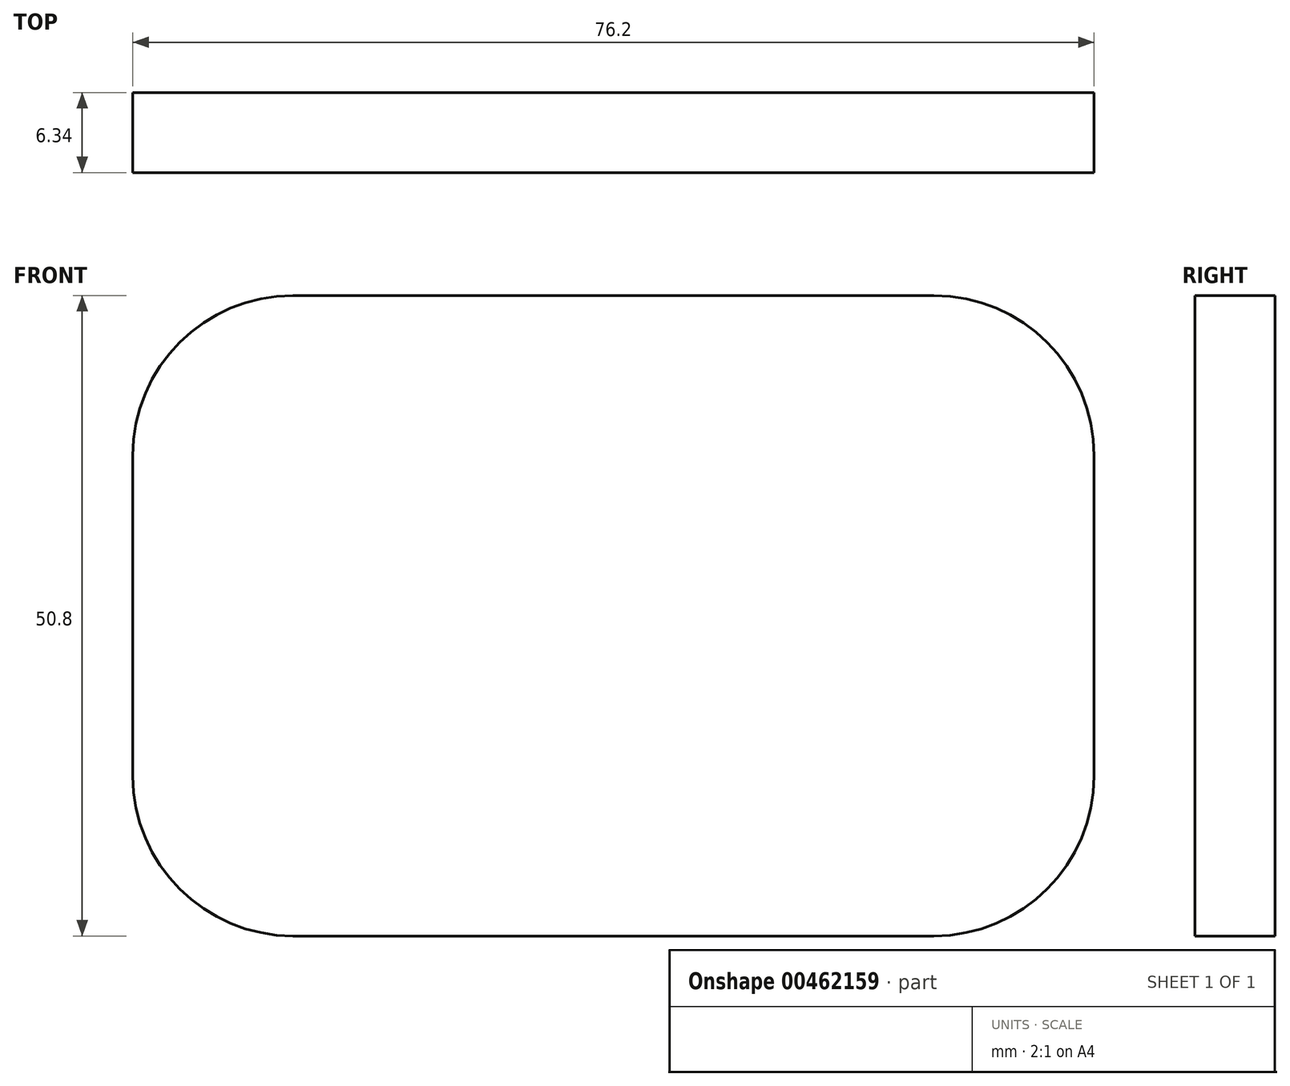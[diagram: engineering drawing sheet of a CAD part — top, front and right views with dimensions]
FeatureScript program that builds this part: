
annotation { "Feature Type Name" : "Feature", "Feature Type Description" : "" }
export const myFeature = defineFeature(function(context is Context, id is Id, definition is map)
    precondition{}
    {
        {
            var Q0;
            Q0=qCreatedBy(makeId("Front.planeOp"),FACE);
            var sketch = newSketch(context, id + "F0", { "sketchPlane" : qUnion([Q0])});
            skLineSegment(sketch, "E0.bottom", {"start": v(25.4, -25.4) * mm, "end": v(-25.4, -25.4) * mm});
            skLineSegment(sketch, "E0.top", {"start": v(25.4, 25.4) * mm, "end": v(-25.4, 25.4) * mm});
            skLineSegment(sketch, "E0.left", {"start": v(38.1, -12.7) * mm, "end": v(38.1, 12.7) * mm});
            skLineSegment(sketch, "E0.right", {"start": v(-38.1, -12.7) * mm, "end": v(-38.1, 12.7) * mm});
            skPoint(sketch, "E0.middle", {"position": v(0, 0) * mm});
            skPoint(sketch, "E1.visualSharp", {"position": v(-38.1, 25.4) * mm});
            skArc(sketch, "E1.filletArc", {"start": v(-25.4, 25.4) * mm, "mid": v(-34.38, 21.68) * mm, "end": v(-38.1, 12.7) * mm});
            skPoint(sketch, "E2.visualSharp", {"position": v(38.1, 25.4) * mm});
            skArc(sketch, "E2.filletArc", {"start": v(38.1, 12.7) * mm, "mid": v(34.38, 21.68) * mm, "end": v(25.4, 25.4) * mm});
            skPoint(sketch, "E3.visualSharp", {"position": v(38.1, -25.4) * mm});
            skArc(sketch, "E3.filletArc", {"start": v(25.4, -25.4) * mm, "mid": v(34.38, -21.68) * mm, "end": v(38.1, -12.7) * mm});
            skPoint(sketch, "E4.visualSharp", {"position": v(-38.1, -25.4) * mm});
            skArc(sketch, "E4.filletArc", {"start": v(-38.1, -12.7) * mm, "mid": v(-34.38, -21.68) * mm, "end": v(-25.4, -25.4) * mm});
            skSolve(sketch);
        }
        {
            var Q0;
            Q0 = qSketchRegion(id + "F0", true);
            extrude(context, id + "F1", {"entities" : qUnion([Q0]), "depth" : 6.35 * mm, "symmetric" : true});
        }
    });
